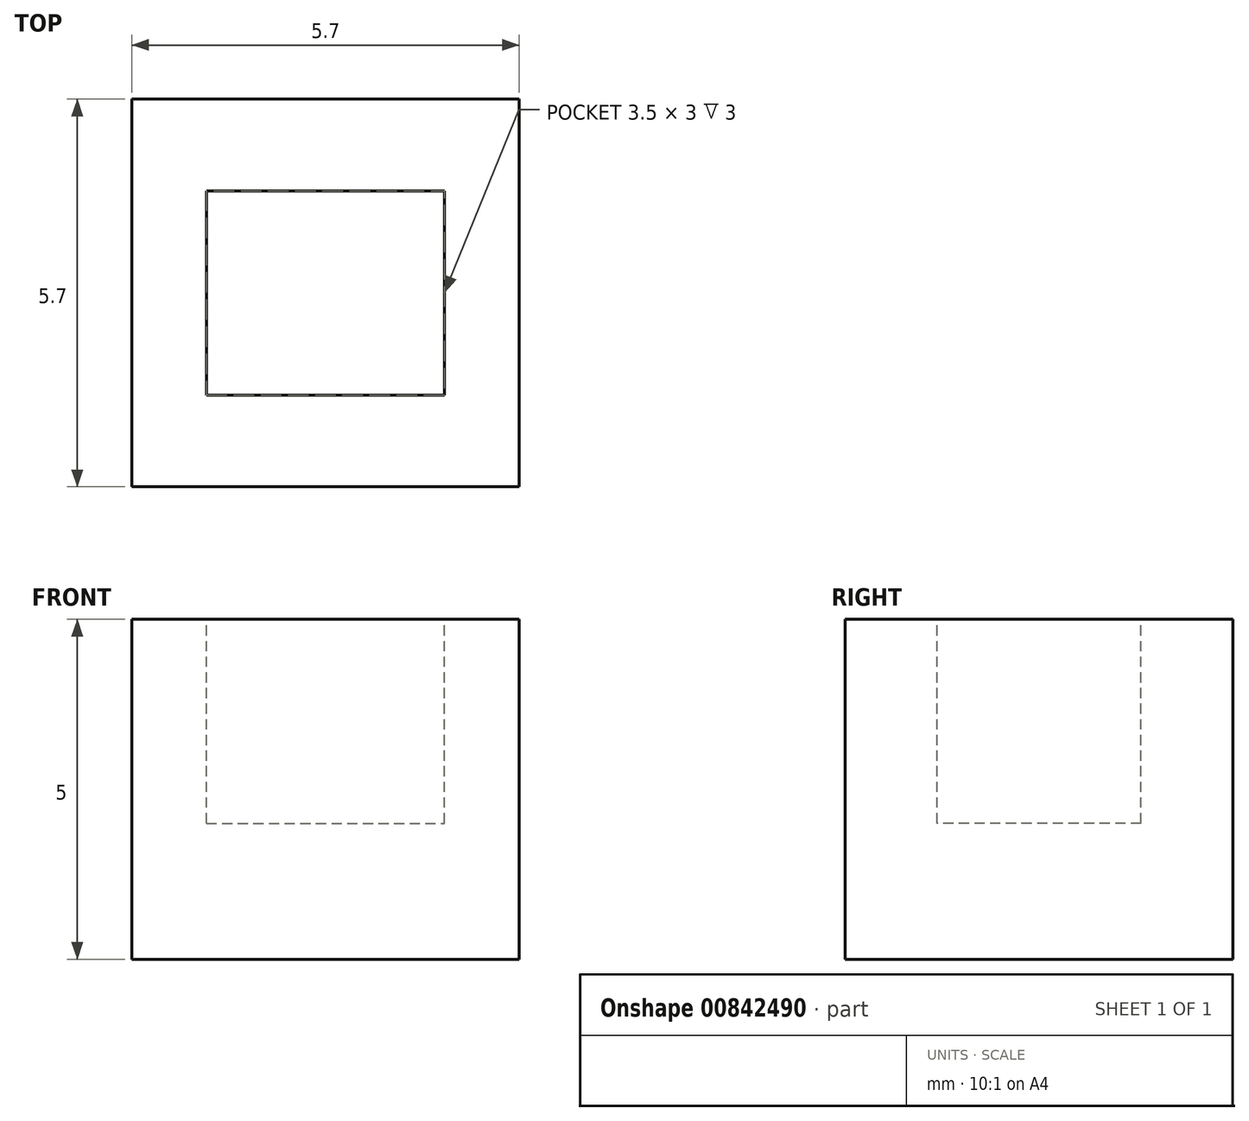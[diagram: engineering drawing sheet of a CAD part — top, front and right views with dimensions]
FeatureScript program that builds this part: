
annotation { "Feature Type Name" : "Feature", "Feature Type Description" : "" }
export const myFeature = defineFeature(function(context is Context, id is Id, definition is map)
    precondition{}
    {
        {
            var Q0;
            Q0=qCreatedBy(makeId("Top.planeOp"),FACE);
            var sketch = newSketch(context, id + "F0", { "sketchPlane" : qUnion([Q0])});
            skLineSegment(sketch, "E0.bottom", {"start": v(0, 0) * mm, "end": v(5.7, 0) * mm});
            skLineSegment(sketch, "E0.top", {"start": v(0, -5.7) * mm, "end": v(5.7, -5.7) * mm});
            skLineSegment(sketch, "E0.left", {"start": v(0, 0) * mm, "end": v(0, -5.7) * mm});
            skLineSegment(sketch, "E0.right", {"start": v(5.7, 0) * mm, "end": v(5.7, -5.7) * mm});
            skSolve(sketch);
        }
        {
            var Q0;
            Q0=makeQuery(id+"F0.imprint","IMPRINT",FACE,{"disambiguationData":[TD([[makeQuery(id+"F0.imprint","IMPRINT",EDGE,{"derivedFrom":sQuery(id+"F0.wireOp",EDGE,"E0.bottom")}),-1.0]])]});
            extrude(context, id + "F1", {"entities" : qUnion([Q0]), "depth" : 5 * mm, "offsetDistance" : 25 * mm});
        }
        {
            var Q0;
            Q0=makeQuery(id+"F1.opExtrude","CAP_FACE",FACE,{"disambiguationData":[OSD([sQuery(id+"F0.wireOp",EDGE,"E0.bottom"),sQuery(id+"F0.wireOp",EDGE,"E0.top"),sQuery(id+"F0.wireOp",EDGE,"E0.left"),sQuery(id+"F0.wireOp",EDGE,"E0.right")])],"isStart":false});
            var sketch = newSketch(context, id + "F2", { "sketchPlane" : qUnion([Q0])});
            skLineSegment(sketch, "E1.bottom", {"start": v(1.1, -1.35) * mm, "end": v(4.6, -1.35) * mm});
            skLineSegment(sketch, "E1.top", {"start": v(1.1, -4.35) * mm, "end": v(4.6, -4.35) * mm});
            skLineSegment(sketch, "E1.left", {"start": v(1.1, -1.35) * mm, "end": v(1.1, -4.35) * mm});
            skLineSegment(sketch, "E1.right", {"start": v(4.6, -1.35) * mm, "end": v(4.6, -4.35) * mm});
            skLineSegment(sketch, "E2", {"start": v(2.85, -5.7) * mm, "end": v(2.85, 0) * mm, "construction": true});
            skLineSegment(sketch, "E3", {"start": v(0, -2.85) * mm, "end": v(5.7, -2.85) * mm, "construction": true});
            skSolve(sketch);
        }
        {
            var Q0;
            Q0=qSketchRegion(id+"F2",true);
            extrude(context, id + "F3", {"entities" : qUnion([Q0]), "operationType" : NewBodyOperationType.REMOVE, "oppositeDirection" : true, "depth" : 3 * mm, "offsetDistance" : 25 * mm});
        }
    });
